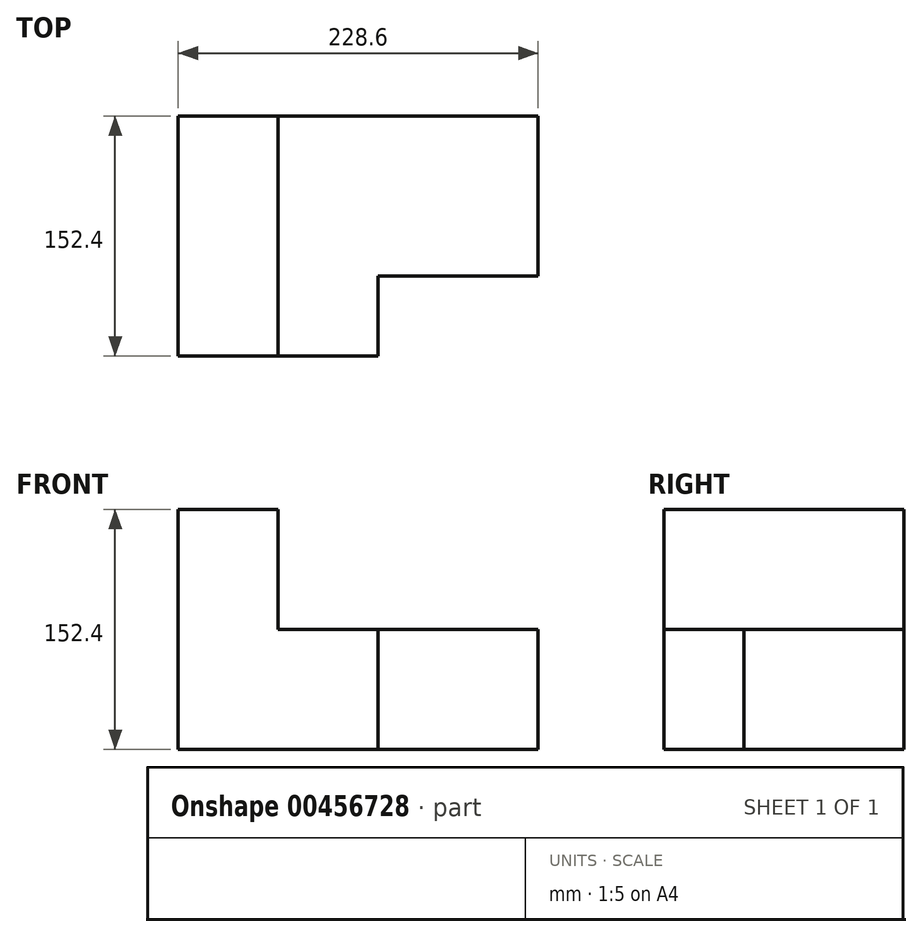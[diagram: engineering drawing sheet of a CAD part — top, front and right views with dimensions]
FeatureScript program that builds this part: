
annotation { "Feature Type Name" : "Feature", "Feature Type Description" : "" }
export const myFeature = defineFeature(function(context is Context, id is Id, definition is map)
    precondition{}
    {
        {
            var Q0;
            Q0=qCreatedBy(makeId("Front.planeOp"),FACE);
            var sketch = newSketch(context, id + "F0", { "sketchPlane" : qUnion([Q0])});
            skLineSegment(sketch, "E0", {"start": v(0, 0) * mm, "end": v(-228.6, 0) * mm});
            skLineSegment(sketch, "E1", {"start": v(-228.6, 0) * mm, "end": v(-228.6, 152.4) * mm});
            skLineSegment(sketch, "E2", {"start": v(-228.6, 152.4) * mm, "end": v(-165.1, 152.4) * mm});
            skLineSegment(sketch, "E3", {"start": v(-165.1, 152.4) * mm, "end": v(-165.1, 76.2) * mm});
            skLineSegment(sketch, "E4", {"start": v(-165.1, 76.2) * mm, "end": v(0, 76.2) * mm});
            skLineSegment(sketch, "E5", {"start": v(0, 76.2) * mm, "end": v(0, 0) * mm});
            skSolve(sketch);
        }
        {
            var Q0;
            Q0=makeQuery(id+"F0.imprint","IMPRINT",FACE,{"disambiguationData":[TD([[makeQuery(id+"F0.imprint","IMPRINT",EDGE,{"derivedFrom":sQuery(id+"F0.wireOp",EDGE,"E0")}),-1.0]])]});
            extrude(context, id + "F1", {"entities" : qUnion([Q0]), "depth" : 152.4 * mm});
        }
        {
            var Q0;
            Q0=makeQuery(id+"F1.opExtrude","CAP_FACE",FACE,{"disambiguationData":[OSD([sQuery(id+"F0.wireOp",EDGE,"E0"),sQuery(id+"F0.wireOp",EDGE,"E1"),sQuery(id+"F0.wireOp",EDGE,"E2"),sQuery(id+"F0.wireOp",EDGE,"E3"),sQuery(id+"F0.wireOp",EDGE,"E4"),sQuery(id+"F0.wireOp",EDGE,"E5")])],"isStart":false});
            var sketch = newSketch(context, id + "F2", { "sketchPlane" : qUnion([Q0])});
            skLineSegment(sketch, "E6", {"start": v(0, 0) * mm, "end": v(0, 76.2) * mm});
            skLineSegment(sketch, "E7", {"start": v(0, 76.2) * mm, "end": v(-101.6, 76.2) * mm});
            skLineSegment(sketch, "E8", {"start": v(-101.6, 76.2) * mm, "end": v(-101.6, 0) * mm});
            skLineSegment(sketch, "E9", {"start": v(-101.6, 0) * mm, "end": v(0, 0) * mm});
            skSolve(sketch);
        }
        {
            var Q0;
            Q0=makeQuery(id+"F2.imprint","IMPRINT",FACE,{"disambiguationData":[TD([[makeQuery(id+"F2.imprint","IMPRINT",EDGE,{"derivedFrom":sQuery(id+"F2.wireOp",EDGE,"E6")}),-1.0]])]});
            extrude(context, id + "F3", {"entities" : qUnion([Q0]), "operationType" : NewBodyOperationType.REMOVE, "oppositeDirection" : true, "depth" : 50.8 * mm});
        }
    });
